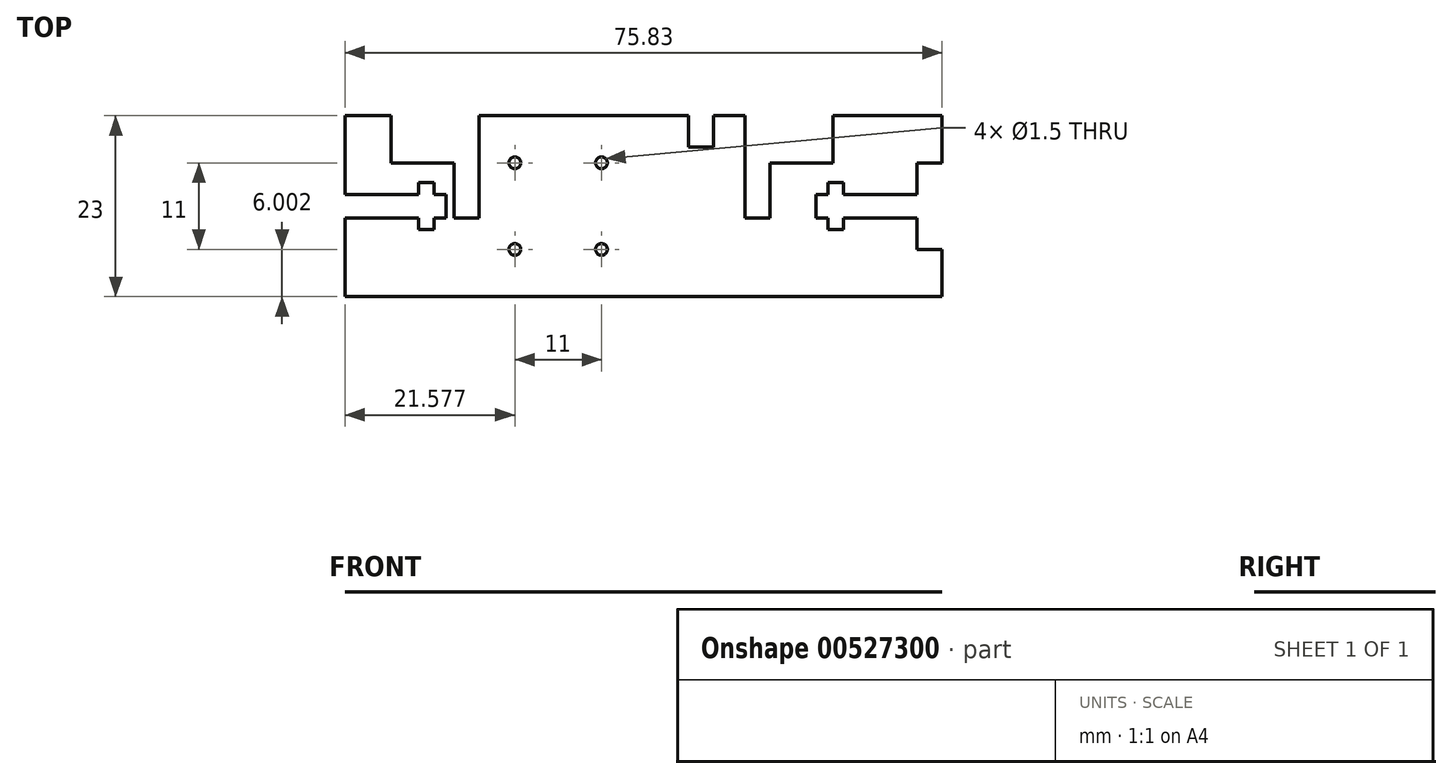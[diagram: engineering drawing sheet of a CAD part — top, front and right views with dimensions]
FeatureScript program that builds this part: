
annotation { "Feature Type Name" : "Feature", "Feature Type Description" : "" }
export const myFeature = defineFeature(function(context is Context, id is Id, definition is map)
    precondition{}
    {
        {
            var Q0;
            Q0=qCreatedBy(makeId("Top.planeOp"),FACE);
            var sketch = newSketch(context, id + "F0", { "sketchPlane" : qUnion([Q0])});
            skCircle(sketch, "E0", {"center": v(-17.18, 31.2) * mm, "radius": 0.75 * mm});
            skLineSegment(sketch, "E1", {"start": v(-16.3, 25.7) * mm, "end": v(-6.18, 25.7) * mm});
            skLineSegment(sketch, "E2", {"start": v(-11.68, 31.97) * mm, "end": v(-11.68, 20.06) * mm});
            skCircle(sketch, "E3.MirrorC", {"center": v(-6.18, 31.2) * mm, "radius": 0.75 * mm});
            skCircle(sketch, "E4.MirrorC", {"center": v(-6.18, 20.2) * mm, "radius": 0.75 * mm});
            skCircle(sketch, "E5.MirrorC", {"center": v(-17.18, 20.2) * mm, "radius": 0.75 * mm});
            skLineSegment(sketch, "E6.bottom", {"start": v(21.07, 27.2) * mm, "end": v(37.07, 27.2) * mm});
            skLineSegment(sketch, "E6.top", {"start": v(21.07, 24.2) * mm, "end": v(37.07, 24.2) * mm});
            skLineSegment(sketch, "E6.left", {"start": v(21.07, 27.2) * mm, "end": v(21.07, 24.2) * mm});
            skLineSegment(sketch, "E6.right", {"start": v(37.07, 27.2) * mm, "end": v(37.07, 24.2) * mm});
            skPoint(sketch, "E6.middle", {"position": v(29.07, 25.7) * mm});
            skLineSegment(sketch, "E7.bottom", {"start": v(37.07, 31.2) * mm, "end": v(33.9, 31.2) * mm});
            skLineSegment(sketch, "E7.top", {"start": v(37.07, 37.2) * mm, "end": v(33.9, 37.2) * mm});
            skLineSegment(sketch, "E7.left", {"start": v(37.07, 31.2) * mm, "end": v(37.07, 37.2) * mm});
            skLineSegment(sketch, "E7.right", {"start": v(33.9, 31.2) * mm, "end": v(33.9, 37.2) * mm});
            skLineSegment(sketch, "E8", {"start": v(29.07, 25.7) * mm, "end": v(41.78, 25.7) * mm});
            skLineSegment(sketch, "E9.MirrorCS", {"start": v(33.9, 20.2) * mm, "end": v(33.9, 14.2) * mm});
            skLineSegment(sketch, "E10.MirrorCS", {"start": v(37.07, 20.2) * mm, "end": v(33.9, 20.2) * mm});
            skLineSegment(sketch, "E11.MirrorCS", {"start": v(37.07, 20.2) * mm, "end": v(37.07, 14.2) * mm});
            skLineSegment(sketch, "E12.MirrorCS", {"start": v(37.07, 14.2) * mm, "end": v(33.9, 14.2) * mm});
            skLineSegment(sketch, "E13", {"start": v(33.9, 20.2) * mm, "end": v(33.9, 31.2) * mm});
            skLineSegment(sketch, "E14.bottom", {"start": v(33.9, 37.2) * mm, "end": v(-41.93, 37.2) * mm});
            skLineSegment(sketch, "E14.top", {"start": v(33.9, 14.2) * mm, "end": v(-41.93, 14.2) * mm});
            skLineSegment(sketch, "E14.left", {"start": v(33.9, 37.2) * mm, "end": v(33.9, 14.2) * mm});
            skLineSegment(sketch, "E14.right", {"start": v(-41.93, 37.2) * mm, "end": v(-41.93, 14.2) * mm});
            skLineSegment(sketch, "E15.bottom", {"start": v(12.07, 37.2) * mm, "end": v(15.24, 37.2) * mm});
            skLineSegment(sketch, "E15.top", {"start": v(12.07, 24.2) * mm, "end": v(15.24, 24.2) * mm});
            skLineSegment(sketch, "E15.left", {"start": v(12.07, 37.2) * mm, "end": v(12.07, 24.2) * mm});
            skLineSegment(sketch, "E15.right", {"start": v(15.24, 37.2) * mm, "end": v(15.24, 24.2) * mm});
            skLineSegment(sketch, "E16.bottom", {"start": v(15.24, 37.2) * mm, "end": v(23.24, 37.2) * mm});
            skLineSegment(sketch, "E16.top", {"start": v(15.24, 31.2) * mm, "end": v(23.24, 31.2) * mm});
            skLineSegment(sketch, "E16.left", {"start": v(15.24, 37.2) * mm, "end": v(15.24, 31.2) * mm});
            skLineSegment(sketch, "E16.right", {"start": v(23.24, 37.2) * mm, "end": v(23.24, 31.2) * mm});
            skLineSegment(sketch, "E17.bottom", {"start": v(22.57, 28.7) * mm, "end": v(24.57, 28.7) * mm});
            skLineSegment(sketch, "E17.top", {"start": v(22.57, 22.7) * mm, "end": v(24.57, 22.7) * mm});
            skLineSegment(sketch, "E17.left", {"start": v(22.57, 28.7) * mm, "end": v(22.57, 22.7) * mm});
            skLineSegment(sketch, "E17.right", {"start": v(24.57, 28.7) * mm, "end": v(24.57, 22.7) * mm});
            skPoint(sketch, "E17.middle", {"position": v(23.57, 25.7) * mm});
            skLineSegment(sketch, "E18.bottom", {"start": v(-41.93, 27.2) * mm, "end": v(-25.93, 27.2) * mm});
            skLineSegment(sketch, "E18.top", {"start": v(-41.93, 24.2) * mm, "end": v(-25.93, 24.2) * mm});
            skLineSegment(sketch, "E18.left", {"start": v(-41.93, 27.2) * mm, "end": v(-41.93, 24.2) * mm});
            skLineSegment(sketch, "E18.right", {"start": v(-25.93, 27.2) * mm, "end": v(-25.93, 24.2) * mm});
            skPoint(sketch, "E18.middle", {"position": v(-33.93, 25.7) * mm});
            skLineSegment(sketch, "E19.bottom", {"start": v(-29.43, 28.7) * mm, "end": v(-27.43, 28.7) * mm});
            skLineSegment(sketch, "E19.top", {"start": v(-29.43, 22.7) * mm, "end": v(-27.43, 22.7) * mm});
            skLineSegment(sketch, "E19.left", {"start": v(-29.43, 28.7) * mm, "end": v(-29.43, 22.7) * mm});
            skLineSegment(sketch, "E19.right", {"start": v(-27.43, 28.7) * mm, "end": v(-27.43, 22.7) * mm});
            skPoint(sketch, "E19.middle", {"position": v(-28.43, 25.7) * mm});
            skLineSegment(sketch, "E20.bottom", {"start": v(-41.93, 31.2) * mm, "end": v(-38.76, 31.2) * mm});
            skLineSegment(sketch, "E20.top", {"start": v(-41.93, 37.2) * mm, "end": v(-38.76, 37.2) * mm});
            skLineSegment(sketch, "E20.left", {"start": v(-41.93, 31.2) * mm, "end": v(-41.93, 37.2) * mm});
            skLineSegment(sketch, "E20.right", {"start": v(-38.76, 31.2) * mm, "end": v(-38.76, 37.2) * mm});
            skLineSegment(sketch, "E21", {"start": v(-28.43, 25.7) * mm, "end": v(-33.93, 25.7) * mm});
            skLineSegment(sketch, "E22.MirrorCS", {"start": v(-38.76, 20.2) * mm, "end": v(-38.76, 14.2) * mm});
            skLineSegment(sketch, "E23.MirrorCS", {"start": v(-41.93, 20.2) * mm, "end": v(-38.76, 20.2) * mm});
            skLineSegment(sketch, "E24", {"start": v(-38.76, 31.2) * mm, "end": v(-38.76, 20.2) * mm});
            skLineSegment(sketch, "E25.bottom", {"start": v(-24.93, 24.2) * mm, "end": v(-21.76, 24.2) * mm});
            skLineSegment(sketch, "E25.top", {"start": v(-24.93, 37.2) * mm, "end": v(-21.76, 37.2) * mm});
            skLineSegment(sketch, "E25.left", {"start": v(-24.93, 24.2) * mm, "end": v(-24.93, 37.2) * mm});
            skLineSegment(sketch, "E25.right", {"start": v(-21.76, 24.2) * mm, "end": v(-21.76, 37.2) * mm});
            skLineSegment(sketch, "E26.bottom", {"start": v(-24.93, 37.2) * mm, "end": v(-32.93, 37.2) * mm});
            skLineSegment(sketch, "E26.top", {"start": v(-24.93, 31.2) * mm, "end": v(-32.93, 31.2) * mm});
            skLineSegment(sketch, "E26.left", {"start": v(-24.93, 37.2) * mm, "end": v(-24.93, 31.2) * mm});
            skLineSegment(sketch, "E26.right", {"start": v(-32.93, 37.2) * mm, "end": v(-32.93, 31.2) * mm});
            skLineSegment(sketch, "E27.bottom", {"start": v(8.07, 37.2) * mm, "end": v(4.9, 37.2) * mm});
            skLineSegment(sketch, "E27.top", {"start": v(8.07, 33.2) * mm, "end": v(4.9, 33.2) * mm});
            skLineSegment(sketch, "E27.left", {"start": v(8.07, 37.2) * mm, "end": v(8.07, 33.2) * mm});
            skLineSegment(sketch, "E27.right", {"start": v(4.9, 37.2) * mm, "end": v(4.9, 33.2) * mm});
            skSolve(sketch);
        }
        {
            var Q0;
            Q0=makeQuery(id+"F0.imprint","IMPRINT",FACE,{"disambiguationData":[TD([[makeQuery(id+"F0.imprint","IMPRINT",EDGE,{"derivedFrom":sQuery(id+"F0.wireOp",EDGE,"E0")}),-1.0]])]});
            var Q1;
            {var subQ0=sQuery(id+"F0.wireOp",EDGE,"E7.bottom");Q1=makeQuery(id+"F0.imprint","IMPRINT",FACE,{"disambiguationData":[TD([[makeQuery(id+"F0.imprint","IMPRINT",EDGE,{"derivedFrom":subQ0}),-1.0]])]});}
            var Q2;
            {var subQ0=sQuery(id+"F0.wireOp",EDGE,"E10.MirrorCS");Q2=makeQuery(id+"F0.imprint","IMPRINT",FACE,{"disambiguationData":[TD([[makeQuery(id+"F0.imprint","IMPRINT",EDGE,{"derivedFrom":subQ0}),1.0]])]});}
            extrude(context, id + "F1", {"entities" : qUnion([Q0, Q1, Q2]), "depth" : 1 / 203.2 * mm, "offsetDistance" : 25 * mm});
        }
    });
